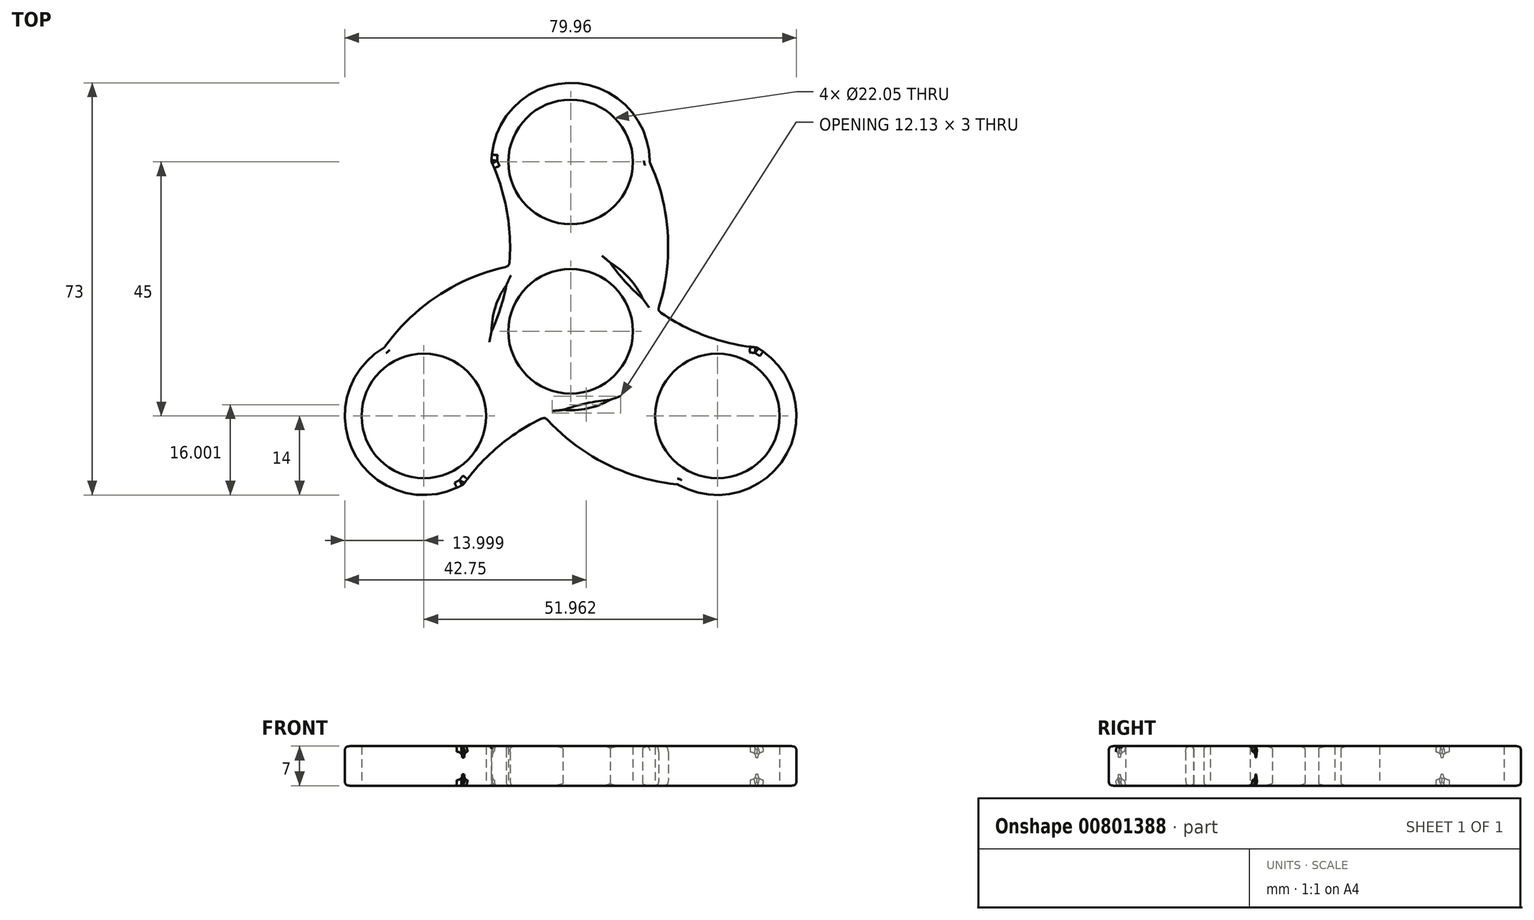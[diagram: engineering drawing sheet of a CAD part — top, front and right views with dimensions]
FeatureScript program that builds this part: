
annotation { "Feature Type Name" : "Feature", "Feature Type Description" : "" }
export const myFeature = defineFeature(function(context is Context, id is Id, definition is map)
    precondition{}
    {
        {
            var Q0;
            Q0=qCreatedBy(makeId("Top.planeOp"),FACE);
            var sketch = newSketch(context, id + "F0", { "sketchPlane" : qUnion([Q0])});
            skCircle(sketch, "E0", {"center": v(0, 0) * mm, "radius": 11.03 * mm});
            skCircle(sketch, "E1", {"center": v(0, 0) * mm, "radius": 14 * mm});
            skLineSegment(sketch, "E2", {"start": v(0, 14) * mm, "end": v(0, 30) * mm, "construction": true});
            skCircle(sketch, "E3", {"center": v(0, 30) * mm, "radius": 11.03 * mm});
            skCircle(sketch, "E4", {"center": v(0, 30) * mm, "radius": 14 * mm});
            skLineSegment(sketch, "E5", {"start": v(0, 30) * mm, "end": v(-14, 30) * mm, "construction": true});
            skLineSegment(sketch, "E6", {"start": v(0, 30) * mm, "end": v(14, 30) * mm, "construction": true});
            skLineSegment(sketch, "E7", {"start": v(-14, 0) * mm, "end": v(14, 0) * mm, "construction": true});
            skArc(sketch, "E8", {"start": v(-14, 0) * mm, "mid": v(-10.73, 15) * mm, "end": v(-14, 30) * mm});
            skArc(sketch, "E9", {"start": v(14, 0) * mm, "mid": v(17.27, 15) * mm, "end": v(14, 30) * mm});
            skCircle(sketch, "E10.1.0", {"center": v(-25.98, -15) * mm, "radius": 11.03 * mm});
            skArc(sketch, "E10.1.1", {"start": v(-7, 12.12) * mm, "mid": v(-21.63, 7.46) * mm, "end": v(-32.98, -2.88) * mm});
            skArc(sketch, "E10.1.2", {"start": v(7, -12.12) * mm, "mid": v(-7.63, -16.79) * mm, "end": v(-18.98, -27.12) * mm});
            skCircle(sketch, "E10.1.3", {"center": v(-25.98, -15) * mm, "radius": 14 * mm});
            skCircle(sketch, "E10.2.0", {"center": v(25.98, -15) * mm, "radius": 11.03 * mm});
            skArc(sketch, "E10.2.1", {"start": v(-7, -12.12) * mm, "mid": v(4.35, -22.46) * mm, "end": v(18.98, -27.12) * mm});
            skArc(sketch, "E10.2.2", {"start": v(7, 12.12) * mm, "mid": v(18.35, 1.79) * mm, "end": v(32.98, -2.88) * mm});
            skCircle(sketch, "E10.2.3", {"center": v(25.98, -15) * mm, "radius": 14 * mm});
            skSolve(sketch);
        }
        {
            var Q0;
            Q0=makeQuery(id+"F0.imprint","IMPRINT",FACE,{"disambiguationData":[TD([[makeQuery(id+"F0.imprint","IMPRINT",EDGE,{"derivedFrom":sQuery(id+"F0.wireOp",EDGE,"E3")}),-1.0]])]});
            var Q1;
            {var subQ7=sQuery(id+"F0.wireOp",EDGE,"E10.2.2");var subQ8=sQuery(id+"F0.wireOp",EDGE,"E1");var subQ9=makeQuery(id+"F0.imprint","INTERSECT",VERTEX,{"disambiguationData":[OD(0.0)],"derivedFrom":[subQ8,subQ7]});Q1=makeQuery(id+"F0.imprint","IMPRINT",FACE,{"disambiguationData":[TD([[makeQuery(id+"F0.imprint","IMPRINT",EDGE,{"disambiguationData":[TD([[subQ9,1.0]])],"derivedFrom":subQ8}),-1.0]])]});}
            var Q2;
            Q2=makeQuery(id+"F0.imprint","IMPRINT",FACE,{"disambiguationData":[TD([[makeQuery(id+"F0.imprint","IMPRINT",EDGE,{"derivedFrom":sQuery(id+"F0.wireOp",EDGE,"E10.2.0")}),-1.0]])]});
            var Q3;
            {var subQ1=sQuery(id+"F0.wireOp",EDGE,"E10.1.2");var subQ3=sQuery(id+"F0.wireOp",EDGE,"E1");var subQ11=makeQuery(id+"F0.imprint","INTERSECT",VERTEX,{"disambiguationData":[OD(0.0)],"derivedFrom":[subQ3,subQ1]});Q3=makeQuery(id+"F0.imprint","IMPRINT",FACE,{"disambiguationData":[TD([[makeQuery(id+"F0.imprint","IMPRINT",EDGE,{"disambiguationData":[TD([[subQ11,1.0]])],"derivedFrom":subQ3}),-1.0]])]});}
            var Q4;
            {var subQ3=sQuery(id+"F0.wireOp",EDGE,"E8");var subQ5=sQuery(id+"F0.wireOp",EDGE,"E1");var subQ6=makeQuery(id+"F0.imprint","INTERSECT",VERTEX,{"disambiguationData":[OD(0.0)],"derivedFrom":[subQ5,subQ3]});Q4=makeQuery(id+"F0.imprint","IMPRINT",FACE,{"disambiguationData":[TD([[makeQuery(id+"F0.imprint","IMPRINT",EDGE,{"disambiguationData":[TD([[subQ6,1.0]])],"derivedFrom":subQ5}),-1.0]])]});}
            var Q5;
            Q5=makeQuery(id+"F0.imprint","IMPRINT",FACE,{"disambiguationData":[TD([[makeQuery(id+"F0.imprint","IMPRINT",EDGE,{"derivedFrom":sQuery(id+"F0.wireOp",EDGE,"E10.1.0")}),-1.0]])]});
            var Q6;
            {var subQ0=sQuery(id+"F0.wireOp",EDGE,"E10.2.1");var subQ1=sQuery(id+"F0.wireOp",EDGE,"E1");var subQ2=makeQuery(id+"F0.imprint","INTERSECT",VERTEX,{"derivedFrom":[subQ1,subQ0]});Q6=makeQuery(id+"F0.imprint","IMPRINT",FACE,{"disambiguationData":[TD([[makeQuery(id+"F0.imprint","IMPRINT",EDGE,{"disambiguationData":[TD([[subQ2,-1.0]])],"derivedFrom":subQ1}),-1.0]])]});}
            var Q7;
            {var subQ0=sQuery(id+"F0.wireOp",EDGE,"E10.1.1");var subQ1=sQuery(id+"F0.wireOp",EDGE,"E1");var subQ2=makeQuery(id+"F0.imprint","INTERSECT",VERTEX,{"derivedFrom":[subQ1,subQ0]});Q7=makeQuery(id+"F0.imprint","IMPRINT",FACE,{"disambiguationData":[TD([[makeQuery(id+"F0.imprint","IMPRINT",EDGE,{"disambiguationData":[TD([[subQ2,-1.0]])],"derivedFrom":subQ1}),-1.0]])]});}
            var Q8;
            Q8=makeQuery(id+"F0.imprint","IMPRINT",FACE,{"disambiguationData":[TD([[makeQuery(id+"F0.imprint","IMPRINT",EDGE,{"derivedFrom":sQuery(id+"F0.wireOp",EDGE,"E0")}),-1.0]])]});
            var Q9;
            {var subQ0=sQuery(id+"F0.wireOp",EDGE,"E9");var subQ1=sQuery(id+"F0.wireOp",EDGE,"E1");var subQ2=makeQuery(id+"F0.imprint","INTERSECT",VERTEX,{"derivedFrom":[subQ1,subQ0]});Q9=makeQuery(id+"F0.imprint","IMPRINT",FACE,{"disambiguationData":[TD([[makeQuery(id+"F0.imprint","IMPRINT",EDGE,{"disambiguationData":[TD([[subQ2,-1.0]])],"derivedFrom":subQ1}),-1.0]])]});}
            extrude(context, id + "F1", {"entities" : qUnion([Q0, Q1, Q2, Q3, Q4, Q5, Q6, Q7, Q8, Q9]), "depth" : 7 * mm, "offsetDistance" : 25 * mm});
        }
        {
            var Q0;
            Q0=makeQuery(id+"F1.opExtrude","SWEPT_FACE",FACE,{"disambiguationData":[OSD([sQuery(id+"F0.wireOp",EDGE,"E9")])]});
            var Q1;
            {var subQ0=sQuery(id+"F0.wireOp",EDGE,"E10.2.3");var subQ1=sQuery(id+"F0.wireOp",EDGE,"E10.2.2");Q1=makeQuery(id+"F1.opExtrude","SWEPT_FACE",FACE,{"disambiguationData":[OSD([subQ1]),TDD([makeQuery(id+"F0.imprint","IMPRINT",EDGE,{"disambiguationData":[TD([[makeQuery(id+"F0.imprint","INTERSECT",VERTEX,{"derivedFrom":[sQuery(id+"F0.wireOp",EDGE,"E9"),subQ1]}),-1.0]])],"derivedFrom":subQ1}),makeQuery(id+"F0.imprint","IMPRINT",EDGE,{"disambiguationData":[TD([[makeQuery(id+"F0.imprint","INTERSECT",VERTEX,{"disambiguationData":[OD(0.0)],"derivedFrom":[subQ1,subQ0]}),1.0]])],"derivedFrom":subQ1})])]});}
            var Q2;
            Q2=makeQuery(id+"F1.opExtrude","SWEPT_FACE",FACE,{"disambiguationData":[OSD([sQuery(id+"F0.wireOp",EDGE,"E10.2.3")])]});
            var Q3;
            Q3=makeQuery(id+"F1.opExtrude","SWEPT_FACE",FACE,{"disambiguationData":[OSD([sQuery(id+"F0.wireOp",EDGE,"E4")])]});
            var Q4;
            {var subQ0=sQuery(id+"F0.wireOp",EDGE,"E8");var subQ1=sQuery(id+"F0.wireOp",EDGE,"E4");var subQ2=makeQuery(id+"F0.imprint","INTERSECT",VERTEX,{"disambiguationData":[OD(1.0)],"derivedFrom":[subQ1,subQ0]});Q4=makeQuery(id+"F1.opExtrude","SWEPT_FACE",FACE,{"disambiguationData":[OSD([subQ0]),TDD([makeQuery(id+"F0.imprint","IMPRINT",EDGE,{"disambiguationData":[TD([[subQ2,1.0]])],"derivedFrom":subQ0}),makeQuery(id+"F0.imprint","IMPRINT",EDGE,{"disambiguationData":[TD([[makeQuery(id+"F0.imprint","INTERSECT",VERTEX,{"disambiguationData":[OD(0.0)],"derivedFrom":[subQ1,subQ0]}),1.0]])],"derivedFrom":subQ0})])]});}
            var Q5;
            Q5=makeQuery(id+"F1.opExtrude","SWEPT_FACE",FACE,{"disambiguationData":[OSD([sQuery(id+"F0.wireOp",EDGE,"E10.1.1")])]});
            var Q6;
            Q6=makeQuery(id+"F1.opExtrude","SWEPT_FACE",FACE,{"disambiguationData":[OSD([sQuery(id+"F0.wireOp",EDGE,"E10.1.3")])]});
            var Q7;
            {var subQ0=sQuery(id+"F0.wireOp",EDGE,"E10.1.3");var subQ1=sQuery(id+"F0.wireOp",EDGE,"E10.1.2");Q7=makeQuery(id+"F1.opExtrude","SWEPT_FACE",FACE,{"disambiguationData":[OSD([subQ1]),TDD([makeQuery(id+"F0.imprint","IMPRINT",EDGE,{"disambiguationData":[TD([[makeQuery(id+"F0.imprint","INTERSECT",VERTEX,{"derivedFrom":[subQ1,sQuery(id+"F0.wireOp",EDGE,"E10.2.1")]}),-1.0]])],"derivedFrom":subQ1}),makeQuery(id+"F0.imprint","IMPRINT",EDGE,{"disambiguationData":[TD([[makeQuery(id+"F0.imprint","INTERSECT",VERTEX,{"disambiguationData":[OD(0.0)],"derivedFrom":[subQ1,subQ0]}),1.0]])],"derivedFrom":subQ1})])]});}
            var Q8;
            Q8=makeQuery(id+"F1.opExtrude","SWEPT_FACE",FACE,{"disambiguationData":[OSD([sQuery(id+"F0.wireOp",EDGE,"E10.2.1")])]});
            fillet(context, id + "F2", {"entities" : qUnion([Q0, Q1, Q2, Q3, Q4, Q5, Q6, Q7, Q8]), "radius" : 1 * mm, "tangentPropagation" : true, "rho" : .6, "crossSection" : FilletCrossSection.CONIC, "allowEdgeOverflow" : false});
        }
        {
            var Q0;
            {var subQ0=sQuery(id+"F0.wireOp",EDGE,"E10.1.2");var subQ1=sQuery(id+"F0.wireOp",EDGE,"E1");Q0=makeQuery(id+"F1.opExtrude","CAP_EDGE",EDGE,{"disambiguationData":[OSD([subQ1]),TDD([makeQuery(id+"F0.imprint","IMPRINT",EDGE,{"disambiguationData":[TD([[makeQuery(id+"F0.imprint","INTERSECT",VERTEX,{"disambiguationData":[OD(0.0)],"derivedFrom":[subQ1,subQ0]}),1.0]])],"derivedFrom":subQ1})])],"isStart":false});}
            var Q1;
            {var subQ0=sQuery(id+"F0.wireOp",EDGE,"E10.1.2");var subQ1=sQuery(id+"F0.wireOp",EDGE,"E1");Q1=makeQuery(id+"F1.opExtrude","CAP_EDGE",EDGE,{"disambiguationData":[OSD([subQ0]),TDD([makeQuery(id+"F0.imprint","IMPRINT",EDGE,{"disambiguationData":[TD([[makeQuery(id+"F0.imprint","INTERSECT",VERTEX,{"disambiguationData":[OD(0.0)],"derivedFrom":[subQ1,subQ0]}),-1.0]])],"derivedFrom":subQ0})])],"isStart":false});}
            var Q2;
            {var subQ0=sQuery(id+"F0.wireOp",EDGE,"E10.2.2");var subQ1=sQuery(id+"F0.wireOp",EDGE,"E1");Q2=makeQuery(id+"F1.opExtrude","CAP_EDGE",EDGE,{"disambiguationData":[OSD([subQ1]),TDD([makeQuery(id+"F0.imprint","IMPRINT",EDGE,{"disambiguationData":[TD([[makeQuery(id+"F0.imprint","INTERSECT",VERTEX,{"disambiguationData":[OD(0.0)],"derivedFrom":[subQ1,subQ0]}),1.0]])],"derivedFrom":subQ1})])],"isStart":false});}
            var Q3;
            {var subQ0=sQuery(id+"F0.wireOp",EDGE,"E10.2.2");var subQ1=sQuery(id+"F0.wireOp",EDGE,"E1");Q3=makeQuery(id+"F1.opExtrude","CAP_EDGE",EDGE,{"disambiguationData":[OSD([subQ0]),TDD([makeQuery(id+"F0.imprint","IMPRINT",EDGE,{"disambiguationData":[TD([[makeQuery(id+"F0.imprint","INTERSECT",VERTEX,{"disambiguationData":[OD(0.0)],"derivedFrom":[subQ1,subQ0]}),-1.0]])],"derivedFrom":subQ0})])],"isStart":false});}
            var Q4;
            {var subQ0=sQuery(id+"F0.wireOp",EDGE,"E8");var subQ1=sQuery(id+"F0.wireOp",EDGE,"E1");Q4=makeQuery(id+"F1.opExtrude","CAP_EDGE",EDGE,{"disambiguationData":[OSD([subQ0]),TDD([makeQuery(id+"F0.imprint","IMPRINT",EDGE,{"disambiguationData":[TD([[makeQuery(id+"F0.imprint","INTERSECT",VERTEX,{"disambiguationData":[OD(0.0)],"derivedFrom":[subQ1,subQ0]}),-1.0]])],"derivedFrom":subQ0})])],"isStart":false});}
            var Q5;
            {var subQ0=sQuery(id+"F0.wireOp",EDGE,"E8");var subQ1=sQuery(id+"F0.wireOp",EDGE,"E1");Q5=makeQuery(id+"F1.opExtrude","CAP_EDGE",EDGE,{"disambiguationData":[OSD([subQ1]),TDD([makeQuery(id+"F0.imprint","IMPRINT",EDGE,{"disambiguationData":[TD([[makeQuery(id+"F0.imprint","INTERSECT",VERTEX,{"disambiguationData":[OD(0.0)],"derivedFrom":[subQ1,subQ0]}),1.0]])],"derivedFrom":subQ1})])],"isStart":false});}
            var Q6;
            {var subQ0=sQuery(id+"F0.wireOp",EDGE,"E10.2.2");var subQ1=sQuery(id+"F0.wireOp",EDGE,"E1");Q6=makeQuery(id+"F1.opExtrude","CAP_EDGE",EDGE,{"disambiguationData":[OSD([subQ0]),TDD([makeQuery(id+"F0.imprint","IMPRINT",EDGE,{"disambiguationData":[TD([[makeQuery(id+"F0.imprint","INTERSECT",VERTEX,{"disambiguationData":[OD(0.0)],"derivedFrom":[subQ1,subQ0]}),-1.0]])],"derivedFrom":subQ0})])],"isStart":true});}
            var Q7;
            {var subQ0=sQuery(id+"F0.wireOp",EDGE,"E10.2.2");var subQ1=sQuery(id+"F0.wireOp",EDGE,"E1");Q7=makeQuery(id+"F1.opExtrude","CAP_EDGE",EDGE,{"disambiguationData":[OSD([subQ1]),TDD([makeQuery(id+"F0.imprint","IMPRINT",EDGE,{"disambiguationData":[TD([[makeQuery(id+"F0.imprint","INTERSECT",VERTEX,{"disambiguationData":[OD(0.0)],"derivedFrom":[subQ1,subQ0]}),1.0]])],"derivedFrom":subQ1})])],"isStart":true});}
            var Q8;
            {var subQ0=sQuery(id+"F0.wireOp",EDGE,"E8");var subQ1=sQuery(id+"F0.wireOp",EDGE,"E1");Q8=makeQuery(id+"F1.opExtrude","CAP_EDGE",EDGE,{"disambiguationData":[OSD([subQ1]),TDD([makeQuery(id+"F0.imprint","IMPRINT",EDGE,{"disambiguationData":[TD([[makeQuery(id+"F0.imprint","INTERSECT",VERTEX,{"disambiguationData":[OD(0.0)],"derivedFrom":[subQ1,subQ0]}),1.0]])],"derivedFrom":subQ1})])],"isStart":true});}
            var Q9;
            {var subQ0=sQuery(id+"F0.wireOp",EDGE,"E8");var subQ1=sQuery(id+"F0.wireOp",EDGE,"E1");Q9=makeQuery(id+"F1.opExtrude","CAP_EDGE",EDGE,{"disambiguationData":[OSD([subQ0]),TDD([makeQuery(id+"F0.imprint","IMPRINT",EDGE,{"disambiguationData":[TD([[makeQuery(id+"F0.imprint","INTERSECT",VERTEX,{"disambiguationData":[OD(0.0)],"derivedFrom":[subQ1,subQ0]}),-1.0]])],"derivedFrom":subQ0})])],"isStart":true});}
            var Q10;
            {var subQ0=sQuery(id+"F0.wireOp",EDGE,"E10.1.2");var subQ1=sQuery(id+"F0.wireOp",EDGE,"E1");Q10=makeQuery(id+"F1.opExtrude","CAP_EDGE",EDGE,{"disambiguationData":[OSD([subQ1]),TDD([makeQuery(id+"F0.imprint","IMPRINT",EDGE,{"disambiguationData":[TD([[makeQuery(id+"F0.imprint","INTERSECT",VERTEX,{"disambiguationData":[OD(0.0)],"derivedFrom":[subQ1,subQ0]}),1.0]])],"derivedFrom":subQ1})])],"isStart":true});}
            var Q11;
            {var subQ0=sQuery(id+"F0.wireOp",EDGE,"E10.1.2");var subQ1=sQuery(id+"F0.wireOp",EDGE,"E1");Q11=makeQuery(id+"F1.opExtrude","CAP_EDGE",EDGE,{"disambiguationData":[OSD([subQ0]),TDD([makeQuery(id+"F0.imprint","IMPRINT",EDGE,{"disambiguationData":[TD([[makeQuery(id+"F0.imprint","INTERSECT",VERTEX,{"disambiguationData":[OD(0.0)],"derivedFrom":[subQ1,subQ0]}),-1.0]])],"derivedFrom":subQ0})])],"isStart":true});}
            fillet(context, id + "F3", {"entities" : qUnion([Q0, Q1, Q2, Q3, Q4, Q5, Q6, Q7, Q8, Q9, Q10, Q11]), "radius" : .5 * mm, "tangentPropagation" : true, "allowEdgeOverflow" : false});
        }
    });
